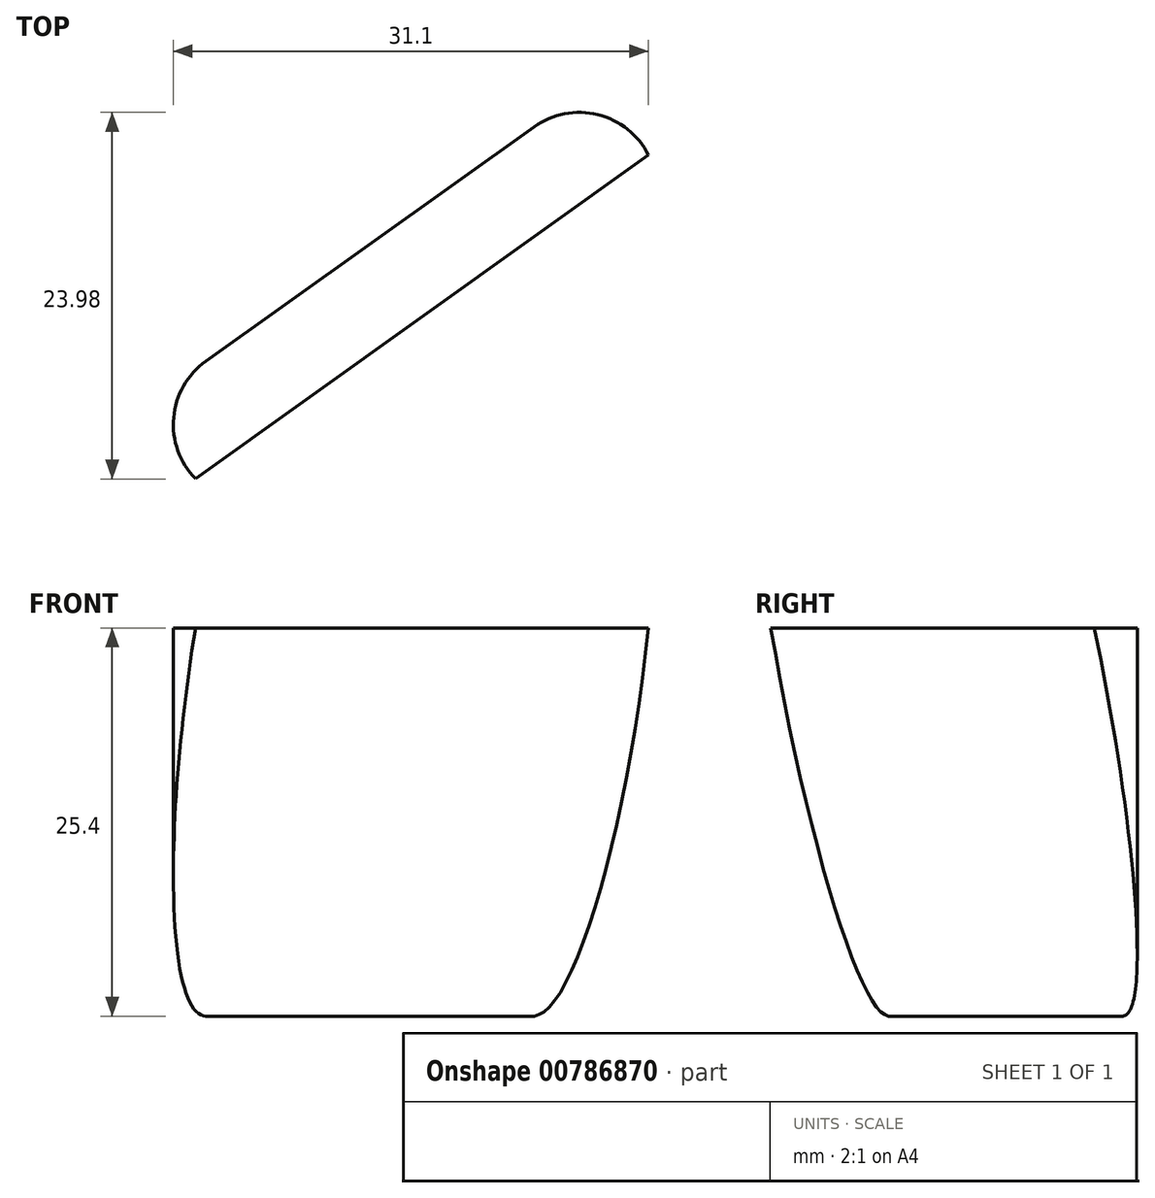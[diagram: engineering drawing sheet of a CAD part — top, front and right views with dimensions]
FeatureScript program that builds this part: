
annotation { "Feature Type Name" : "Feature", "Feature Type Description" : "" }
export const myFeature = defineFeature(function(context is Context, id is Id, definition is map)
    precondition{}
    {
        {
            var Q0;
            Q0=qCreatedBy(makeId("Top.planeOp"),FACE);
            var sketch = newSketch(context, id + "F0", { "sketchPlane" : qUnion([Q0])});
            skLineSegment(sketch, "E0.bottom", {"start": v(0, 0) * mm, "end": v(25.4, 0) * mm});
            skLineSegment(sketch, "E0.top", {"start": v(0, 25.4) * mm, "end": v(25.4, 25.4) * mm});
            skLineSegment(sketch, "E0.left", {"start": v(0, 0) * mm, "end": v(0, 25.4) * mm});
            skLineSegment(sketch, "E0.right", {"start": v(25.4, 0) * mm, "end": v(25.4, 25.4) * mm});
            skCircle(sketch, "E1.cCircle", {"center": v(10.4, -28.9) * mm, "radius": 12.7 * mm, "construction": true});
            skLineSegment(sketch, "E1.0", {"start": v(-7.72, -26.23) * mm, "end": v(13.76, -10.88) * mm});
            skLineSegment(sketch, "E1.1", {"start": v(21.77, -14.53) * mm, "end": v(24.32, -40.8) * mm});
            skLineSegment(sketch, "E1.2", {"start": v(17.16, -45.92) * mm, "end": v(-6.87, -34.98) * mm});
            skPoint(sketch, "E1.0.midPoint", {"position": v(3.02, -18.56) * mm});
            skCircle(sketch, "E2", {"center": v(8.98, 61.2) * mm, "radius": 14.93 * mm});
            skPoint(sketch, "E3.visualSharp", {"position": v(-14.88, -31.34) * mm});
            skArc(sketch, "E3.filletArc", {"start": v(-7.72, -26.23) * mm, "mid": v(-9.82, -30.85) * mm, "end": v(-6.87, -34.98) * mm});
            skPoint(sketch, "E4.visualSharp", {"position": v(20.92, -5.77) * mm});
            skArc(sketch, "E4.filletArc", {"start": v(21.77, -14.53) * mm, "mid": v(18.82, -10.4) * mm, "end": v(13.76, -10.88) * mm});
            skPoint(sketch, "E5.visualSharp", {"position": v(25.17, -49.56) * mm});
            skArc(sketch, "E5.filletArc", {"start": v(17.16, -45.92) * mm, "mid": v(22.21, -45.43) * mm, "end": v(24.32, -40.8) * mm});
            skCircle(sketch, "E6", {"center": v(10.4, -28.9) * mm, "radius": 20.32 * mm});
            skSolve(sketch);
        }
        {
            var Q0;
            Q0=qCreatedBy(makeId("Top.planeOp"),FACE);
            cPlane(context, id + "F1", {"entities" : qUnion([Q0]), "cplaneType" : CPlaneType.OFFSET, "offset" : 28.7 * mm, "width" : 152.4 * mm, "height" : 152.4 * mm});
        }
        {
            var Q0;
            Q0=qCreatedBy(id+"F1.planeOp",FACE);
            var sketch = newSketch(context, id + "F2", { "sketchPlane" : qUnion([Q0])});
            skCircle(sketch, "E7", {"center": v(10.4, -28.9) * mm, "radius": 0.13 * mm});
            skSolve(sketch);
        }
        {
            var Q0;
            Q0=makeQuery(id+"F0.imprint","IMPRINT",FACE,{"disambiguationData":[TD([[makeQuery(id+"F0.imprint","IMPRINT",EDGE,{"derivedFrom":sQuery(id+"F0.wireOp",EDGE,"E1.0")}),-1.0]])]});
            var Q1;
            Q1=sQuery(id+"F2.wireOp",VERTEX,"E7.center");
            loft(context, id + "F3", {"sheetProfilesArray" : [{ "sheetProfileEntities" : qUnion([Q0]) }, { "sheetProfileEntities" : qUnion([Q1]) }]});
        }
        {
            var Q0;
            Q0=makeQuery(id+"F0.imprint","IMPRINT",FACE,{"disambiguationData":[TD([[makeQuery(id+"F0.imprint","IMPRINT",EDGE,{"derivedFrom":sQuery(id+"F0.wireOp",EDGE,"E1.0")}),-1.0]])]});
            extrude(context, id + "F4", {"entities" : qUnion([Q0]), "oppositeDirection" : true, "depth" : 48 * mm, "offsetDistance" : 25.4 * mm, "hasSecondDirection" : true, "secondDirectionOppositeDirection" : false, "secondDirectionDepth" : 25.4 * mm});
        }
        {
            var Q0;
            {var subQ0=sQuery(id+"F0.wireOp",EDGE,"E1.0");Q0=makeQuery(id+"F0.imprint","IMPRINT",FACE,{"disambiguationData":[TD([[makeQuery(id+"F0.imprint","IMPRINT",EDGE,{"derivedFrom":subQ0}),1.0]])]});}
            extrude(context, id + "F5", {"entities" : qUnion([Q0]), "operationType" : NewBodyOperationType.INTERSECT, "depth" : 25.4 * mm, "offsetDistance" : 25.4 * mm, "hasDraft" : true, "draftAngle" : 13 * degree});
        }
    });
